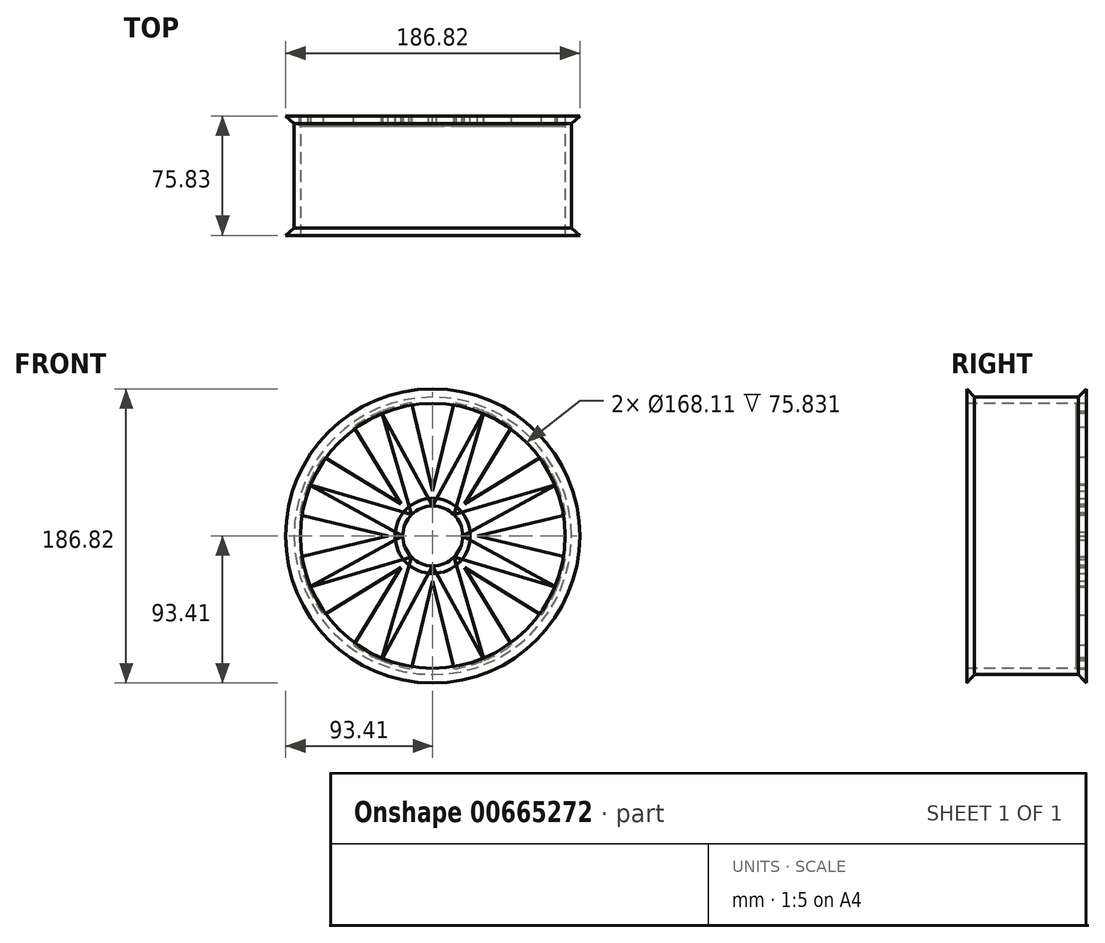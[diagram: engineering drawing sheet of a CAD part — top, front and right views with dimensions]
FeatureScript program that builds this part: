
annotation { "Feature Type Name" : "Feature", "Feature Type Description" : "" }
export const myFeature = defineFeature(function(context is Context, id is Id, definition is map)
    precondition{}
    {
        {
            var Q0;
            Q0=qCreatedBy(makeId("Front.planeOp"),FACE);
            var sketch = newSketch(context, id + "F0", { "sketchPlane" : qUnion([Q0])});
            skCircle(sketch, "E0", {"center": v(0, 0) * mm, "radius": 19.05 * mm});
            skLineSegment(sketch, "E1", {"start": v(0, 28.49) * mm, "end": v(13.45, 84.48) * mm});
            skLineSegment(sketch, "E2", {"start": v(-13.46, 84.48) * mm, "end": v(0, 28.49) * mm});
            skCircle(sketch, "E3", {"center": v(0, 0) * mm, "radius": 85.55 * mm});
            skLineSegment(sketch, "E4.1.0", {"start": v(-20.14, 20.14) * mm, "end": v(-50.23, 69.25) * mm});
            skLineSegment(sketch, "E4.1.1", {"start": v(-69.26, 50.22) * mm, "end": v(-20.14, 20.14) * mm});
            skLineSegment(sketch, "E4.2.0", {"start": v(-28.49, 0) * mm, "end": v(-84.48, 13.45) * mm});
            skLineSegment(sketch, "E4.2.1", {"start": v(-84.48, -13.46) * mm, "end": v(-28.49, 0) * mm});
            skLineSegment(sketch, "E4.3.0", {"start": v(-20.14, -20.14) * mm, "end": v(-69.25, -50.23) * mm});
            skLineSegment(sketch, "E4.3.1", {"start": v(-50.22, -69.26) * mm, "end": v(-20.14, -20.14) * mm});
            skLineSegment(sketch, "E4.4.0", {"start": v(0, -28.49) * mm, "end": v(-13.45, -84.48) * mm});
            skLineSegment(sketch, "E4.4.1", {"start": v(13.46, -84.48) * mm, "end": v(0, -28.49) * mm});
            skLineSegment(sketch, "E4.5.0", {"start": v(20.14, -20.14) * mm, "end": v(50.23, -69.25) * mm});
            skLineSegment(sketch, "E4.5.1", {"start": v(69.26, -50.22) * mm, "end": v(20.14, -20.14) * mm});
            skLineSegment(sketch, "E4.6.0", {"start": v(28.49, 0) * mm, "end": v(84.48, -13.45) * mm});
            skLineSegment(sketch, "E4.6.1", {"start": v(84.48, 13.46) * mm, "end": v(28.49, 0) * mm});
            skLineSegment(sketch, "E4.7.0", {"start": v(20.14, 20.14) * mm, "end": v(69.25, 50.23) * mm});
            skLineSegment(sketch, "E4.7.1", {"start": v(50.22, 69.26) * mm, "end": v(20.14, 20.14) * mm});
            skSolve(sketch);
        }
        {
            var Q0;
            Q0=makeQuery(id+"F0.imprint","IMPRINT",FACE,{"disambiguationData":[TD([[makeQuery(id+"F0.imprint","IMPRINT",EDGE,{"derivedFrom":sQuery(id+"F0.wireOp",EDGE,"E0")}),-1.0]])]});
            extrude(context, id + "F1", {"entities" : qUnion([Q0]), "depth" : 6.35 * mm, "offsetDistance" : 25.4 * mm});
        }
        {
            var Q0;
            Q0=makeQuery(id+"F1.opExtrude","CAP_FACE",FACE,{"disambiguationData":[OSD([sQuery(id+"F0.wireOp",EDGE,"E0"),sQuery(id+"F0.wireOp",EDGE,"E1"),sQuery(id+"F0.wireOp",EDGE,"E2"),sQuery(id+"F0.wireOp",EDGE,"E3"),sQuery(id+"F0.wireOp",EDGE,"E4.1.0"),sQuery(id+"F0.wireOp",EDGE,"E4.1.1"),sQuery(id+"F0.wireOp",EDGE,"E4.2.0"),sQuery(id+"F0.wireOp",EDGE,"E4.2.1"),sQuery(id+"F0.wireOp",EDGE,"E4.3.0"),sQuery(id+"F0.wireOp",EDGE,"E4.3.1"),sQuery(id+"F0.wireOp",EDGE,"E4.4.0"),sQuery(id+"F0.wireOp",EDGE,"E4.4.1"),sQuery(id+"F0.wireOp",EDGE,"E4.5.0"),sQuery(id+"F0.wireOp",EDGE,"E4.5.1"),sQuery(id+"F0.wireOp",EDGE,"E4.6.0"),sQuery(id+"F0.wireOp",EDGE,"E4.6.1"),sQuery(id+"F0.wireOp",EDGE,"E4.7.0"),sQuery(id+"F0.wireOp",EDGE,"E4.7.1")])],"isStart":false});
            var sketch = newSketch(context, id + "F2", { "sketchPlane" : qUnion([Q0])});
            skLineSegment(sketch, "E5", {"start": v(0, 19.05) * mm, "end": v(32.73, 79.04) * mm});
            skLineSegment(sketch, "E6", {"start": v(32.73, 79.04) * mm, "end": v(13.48, 13.46) * mm});
            skLineSegment(sketch, "E7", {"start": v(13.48, 13.46) * mm, "end": v(79.03, 32.74) * mm});
            skLineSegment(sketch, "E8", {"start": v(79.03, 32.74) * mm, "end": v(19.05, 0) * mm});
            skLineSegment(sketch, "E9", {"start": v(19.05, 0) * mm, "end": v(79.04, -32.73) * mm});
            skLineSegment(sketch, "E10", {"start": v(79.04, -32.73) * mm, "end": v(13.46, -13.48) * mm});
            skLineSegment(sketch, "E11", {"start": v(13.46, -13.48) * mm, "end": v(32.74, -79.03) * mm});
            skLineSegment(sketch, "E12", {"start": v(32.74, -79.03) * mm, "end": v(0, -19.05) * mm});
            skLineSegment(sketch, "E13", {"start": v(0, -19.05) * mm, "end": v(-32.73, -79.04) * mm});
            skLineSegment(sketch, "E14", {"start": v(-32.73, -79.04) * mm, "end": v(-13.48, -13.46) * mm});
            skLineSegment(sketch, "E15", {"start": v(-13.48, -13.46) * mm, "end": v(-79.03, -32.74) * mm});
            skLineSegment(sketch, "E16", {"start": v(-79.03, -32.74) * mm, "end": v(-19.05, 0) * mm});
            skLineSegment(sketch, "E17", {"start": v(-19.05, 0) * mm, "end": v(-79.04, 32.73) * mm});
            skLineSegment(sketch, "E18", {"start": v(-79.04, 32.73) * mm, "end": v(-13.46, 13.48) * mm});
            skLineSegment(sketch, "E19", {"start": v(-13.46, 13.48) * mm, "end": v(-32.74, 79.04) * mm});
            skLineSegment(sketch, "E20", {"start": v(-32.74, 79.04) * mm, "end": v(0, 19.05) * mm});
            skSolve(sketch);
        }
        {
            var Q0;
            {var subQ0=sQuery(id+"F2.wireOp",EDGE,"E7");Q0=makeQuery(id+"F2.imprint","IMPRINT",FACE,{"disambiguationData":[TD([[makeQuery(id+"F2.imprint","IMPRINT",EDGE,{"derivedFrom":subQ0}),-1.0]])]});}
            var Q1;
            {var subQ0=sQuery(id+"F2.wireOp",EDGE,"E5");Q1=makeQuery(id+"F2.imprint","IMPRINT",FACE,{"disambiguationData":[TD([[makeQuery(id+"F2.imprint","IMPRINT",EDGE,{"derivedFrom":subQ0}),-1.0]])]});}
            var Q2;
            {var subQ1=makeQuery(id+"F1.opExtrude","CAP_EDGE",EDGE,{"disambiguationData":[OSD([sQuery(id+"F0.wireOp",EDGE,"E0")])],"isStart":false});var subQ6=sQuery(id+"F2.wireOp",EDGE,"E20");var subQ7=makeQuery(id+"F2.imprint","INTERSECT",VERTEX,{"derivedFrom":[subQ1,sQuery(id+"F2.wireOp",EDGE,"E5"),subQ6]});Q2=makeQuery(id+"F2.imprint","IMPRINT",FACE,{"disambiguationData":[TD([[makeQuery(id+"F2.imprint","IMPRINT",EDGE,{"disambiguationData":[TD([[subQ7,-1.0]])],"derivedFrom":subQ1}),-1.0]])]});}
            var Q3;
            {var subQ0=sQuery(id+"F2.wireOp",EDGE,"E17");Q3=makeQuery(id+"F2.imprint","IMPRINT",FACE,{"disambiguationData":[TD([[makeQuery(id+"F2.imprint","IMPRINT",EDGE,{"derivedFrom":subQ0}),-1.0]])]});}
            var Q4;
            {var subQ0=sQuery(id+"F2.wireOp",EDGE,"E15");Q4=makeQuery(id+"F2.imprint","IMPRINT",FACE,{"disambiguationData":[TD([[makeQuery(id+"F2.imprint","IMPRINT",EDGE,{"derivedFrom":subQ0}),-1.0]])]});}
            var Q5;
            {var subQ0=sQuery(id+"F2.wireOp",EDGE,"E13");Q5=makeQuery(id+"F2.imprint","IMPRINT",FACE,{"disambiguationData":[TD([[makeQuery(id+"F2.imprint","IMPRINT",EDGE,{"derivedFrom":subQ0}),-1.0]])]});}
            var Q6;
            {var subQ0=sQuery(id+"F2.wireOp",EDGE,"E11");Q6=makeQuery(id+"F2.imprint","IMPRINT",FACE,{"disambiguationData":[TD([[makeQuery(id+"F2.imprint","IMPRINT",EDGE,{"derivedFrom":subQ0}),-1.0]])]});}
            var Q7;
            {var subQ0=sQuery(id+"F2.wireOp",EDGE,"E9");Q7=makeQuery(id+"F2.imprint","IMPRINT",FACE,{"disambiguationData":[TD([[makeQuery(id+"F2.imprint","IMPRINT",EDGE,{"derivedFrom":subQ0}),-1.0]])]});}
            extrude(context, id + "F3", {"entities" : qUnion([Q0, Q1, Q2, Q3, Q4, Q5, Q6, Q7]), "operationType" : NewBodyOperationType.REMOVE, "oppositeDirection" : true, "depth" : 25.4 * mm, "offsetDistance" : 25.4 * mm});
        }
        {
            var Q0;
            Q0=qCreatedBy(makeId("Front.planeOp"),FACE);
            var sketch = newSketch(context, id + "F4", { "sketchPlane" : qUnion([Q0])});
            skCircle(sketch, "E21", {"center": v(0, 0) * mm, "radius": 23.86 * mm});
            skSolve(sketch);
        }
        {
            var Q0;
            Q0=makeQuery(id+"F4.imprint","IMPRINT",FACE,{"disambiguationData":[TD([[makeQuery(id+"F4.imprint","IMPRINT",EDGE,{"derivedFrom":sQuery(id+"F4.wireOp",EDGE,"E21")}),1.0]])]});
            extrude(context, id + "F5", {"entities" : qUnion([Q0]), "depth" : 6.35 * mm, "offsetDistance" : 25.4 * mm});
        }
        {
            var Q0;
            Q0=qCreatedBy(makeId("Right.planeOp"),FACE);
            var sketch = newSketch(context, id + "F6", { "sketchPlane" : qUnion([Q0])});
            skLineSegment(sketch, "E22", {"start": v(0, 93.41) * mm, "end": v(0, 84.05) * mm});
            skLineSegment(sketch, "E23", {"start": v(0, 84.05) * mm, "end": v(-75.83, 84.05) * mm});
            skLineSegment(sketch, "E24", {"start": v(-75.83, 84.05) * mm, "end": v(-75.83, 93.4) * mm});
            skLineSegment(sketch, "E25", {"start": v(-75.83, 93.4) * mm, "end": v(-71.04, 88.09) * mm});
            skLineSegment(sketch, "E26", {"start": v(0, 93.41) * mm, "end": v(-4.89, 88.09) * mm});
            skLineSegment(sketch, "E27", {"start": v(-71.04, 88.09) * mm, "end": v(-4.89, 88.09) * mm});
            skSolve(sketch);
        }
        {
            var Q0;
            Q0=qCreatedBy(makeId("Top.planeOp"),FACE);
            var sketch = newSketch(context, id + "F7", { "sketchPlane" : qUnion([Q0])});
            skLineSegment(sketch, "E28", {"start": v(0, 0) * mm, "end": v(0, 80.06) * mm});
            skSolve(sketch);
        }
        {
            var Q0;
            Q0=makeQuery(id+"F6.imprint","IMPRINT",FACE,{"disambiguationData":[TD([[makeQuery(id+"F6.imprint","IMPRINT",EDGE,{"derivedFrom":sQuery(id+"F6.wireOp",EDGE,"E22")}),-1.0]])]});
            var Q1;
            Q1=sQuery(id+"F7.wireOp",EDGE,"E28");
            revolve(context, id + "F8", {"entities" : qUnion([Q0]), "axis" : qUnion([Q1]), "revolveType" : RevolveType.FULL});
        }
    });
